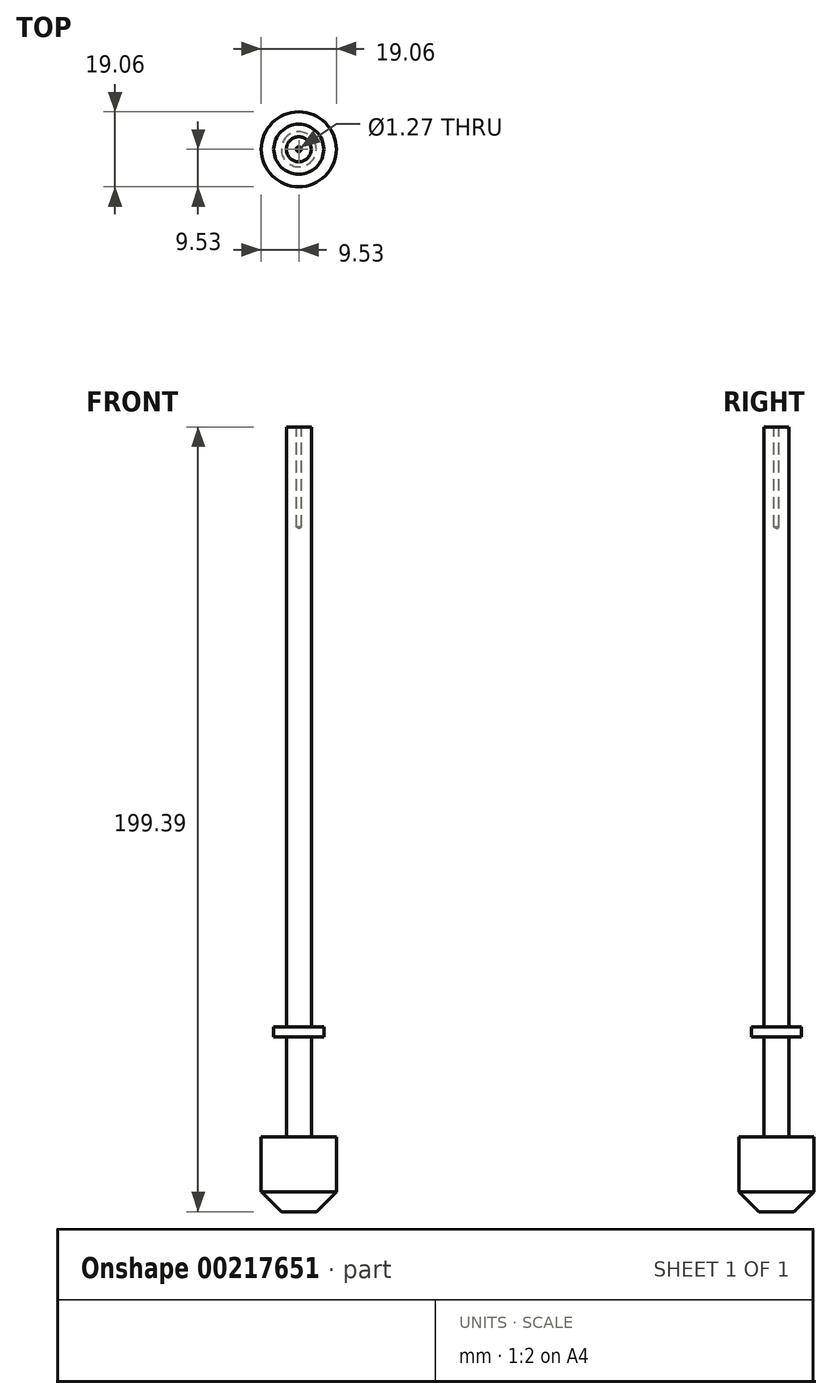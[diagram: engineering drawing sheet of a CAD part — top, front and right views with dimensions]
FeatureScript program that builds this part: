
annotation { "Feature Type Name" : "Feature", "Feature Type Description" : "" }
export const myFeature = defineFeature(function(context is Context, id is Id, definition is map)
    precondition{}
    {
        {
            var Q0;
            Q0=qCreatedBy(makeId("Top.planeOp"),FACE);
            var sketch = newSketch(context, id + "F0", { "sketchPlane" : qUnion([Q0])});
            skCircle(sketch, "E0", {"center": v(0, 0) * mm, "radius": 3.18 * mm});
            skSolve(sketch);
        }
        {
            var Q0;
            Q0 = qSketchRegion(id + "F0", true);
            extrude(context, id + "F1", {"entities" : qUnion([Q0]), "depth" : 152.4 * mm});
        }
        {
            var Q0;
            Q0=makeQuery(id+"F1.opExtrude","CAP_FACE",FACE,{"disambiguationData":[OSD([sQuery(id+"F0.wireOp",EDGE,"E0")])],"isStart":true});
            var sketch = newSketch(context, id + "F2", { "sketchPlane" : qUnion([Q0])});
            skCircle(sketch, "E1", {"center": v(0, 0) * mm, "radius": 6.35 * mm});
            skSolve(sketch);
        }
        {
            var Q0;
            Q0 = qSketchRegion(id + "F2", true);
            extrude(context, id + "F3", {"entities" : qUnion([Q0]), "operationType" : NewBodyOperationType.ADD, "depth" : 2.54 * mm});
        }
        {
            var Q0;
            Q0=makeQuery(id+"F3.opExtrude","CAP_FACE",FACE,{"disambiguationData":[OSD([sQuery(id+"F2.wireOp",EDGE,"E1")])],"isStart":false});
            var sketch = newSketch(context, id + "F4", { "sketchPlane" : qUnion([Q0])});
            skCircle(sketch, "E2", {"center": v(0, 0) * mm, "radius": 3.18 * mm});
            skSolve(sketch);
        }
        {
            var Q0;
            Q0 = qSketchRegion(id + "F4", true);
            extrude(context, id + "F5", {"entities" : qUnion([Q0]), "operationType" : NewBodyOperationType.ADD, "depth" : 25.4 * mm});
        }
        {
            var Q0;
            Q0=makeQuery(id+"F5.opExtrude","CAP_FACE",FACE,{"disambiguationData":[OSD([sQuery(id+"F4.wireOp",EDGE,"E2")])],"isStart":false});
            var sketch = newSketch(context, id + "F6", { "sketchPlane" : qUnion([Q0])});
            skCircle(sketch, "E3", {"center": v(0, 0) * mm, "radius": 9.53 * mm});
            skSolve(sketch);
        }
        {
            var Q0;
            Q0 = qSketchRegion(id + "F6", true);
            extrude(context, id + "F7", {"entities" : qUnion([Q0]), "operationType" : NewBodyOperationType.ADD, "depth" : 19.05 * mm});
        }
        {
            var Q0;
            Q0=makeQuery(id+"F7.opExtrude","CAP_EDGE",EDGE,{"disambiguationData":[OSD([sQuery(id+"F6.wireOp",EDGE,"E3")])],"isStart":false});
            chamfer(context, id + "F8", {"entities" : qUnion([Q0]), "width" : 5.08 * mm, "tangentPropagation" : true});
        }
        {
            var Q0;
            Q0=makeQuery(id+"F1.opExtrude","CAP_FACE",FACE,{"disambiguationData":[OSD([sQuery(id+"F0.wireOp",EDGE,"E0")])],"isStart":false});
            var sketch = newSketch(context, id + "F9", { "sketchPlane" : qUnion([Q0])});
            skPoint(sketch, "E4", {"position": v(0, 0) * mm});
            skSolve(sketch);
        }
        {
            var Q0;
            Q0=sQuery(id+"F9.wireOp",VERTEX,"E4");
            var Q1;
            Q1=makeQuery(id+"F1.opExtrude","SWEPT_BODY",BODY,{"disambiguationData":[OSD([sQuery(id+"F0.wireOp",EDGE,"E0")])]});
            hole(context, id + "F10", {"style" : HoleStyle.SIMPLE, "endStyle" : HoleEndStyle.BLIND, "holeDiameter" : 1.27 * mm, "holeDepth" : 25.4 * mm, "locations" : qUnion([Q0]), "scope" : qUnion([Q1])});
        }
    });
